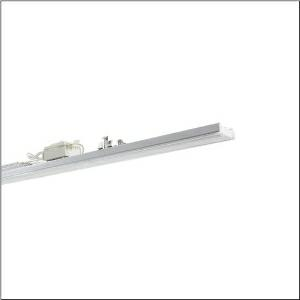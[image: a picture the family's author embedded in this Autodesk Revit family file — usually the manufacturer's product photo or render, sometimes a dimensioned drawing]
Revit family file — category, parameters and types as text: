
# Revit family: licross_r__11_recessed_ho_51tl1emv4g5s_f904
name_source: partatom
category: Lighting Fixtures
units: mm (PartAtom-declared; Revit-internal decimal feet)

## family parameters
Cut with Voids When Loaded = No
Host = Face
Light Source = No
Part Type = Normal
Room Calculation Point = No
Round Connector Dimension = Use Diameter
Shared = No

## types (1)
- --- (1 x LED, 16830 lm, 89.2 W, 4000K)
    Apparent Load = 89 VA
    CIE Flux Codes = 85 95 99 100 100
    Color Rendering = 80
    Color Temperature = 4000K
    Default Elevation = 1800 mm
    Description = Licross® 11 Recessed HO, luminaire insert, of sheet steel, coil coated, white, length: 2.250mm, width: 66mm, height: 67mm, LED rated luminous flux: 16.830lm, light colour: 840, control gear: ON/OFF Multilumen, with plug, 3-pole, with phase selection, mains connection: 220..240V, AC, 50/60Hz, rated input power: 89W, internal wiring halogen-free, primary light control with lens, of plastic, primary optical cover: cover, of PMMA, light emission: direct distribution, primary light characteristic: symmetric, protection rating (complete): IP40, insulation class (complete): insulation class I (protective earthing), certification: CE, ENEC, VDE, UKCA, protection symbol: D if used in an environment without relevant dust loads with corresponding accessories, impact resistance: IK06, permissible ambient temperature for indoor applications: -35..+35°C, corresponds to IFS (International Featured Standards) requirements for safety and quality in the food industry, reducing of maximum allowable ambient temperature of 5°C with ceiling mounting, packaging unit: 1 piece
    Height = 58 mm
    Lamp = 1 x LED
    Lamp Light Flux = 16830 lm
    Lamp Power = 89.2 W
    Lamp count = 1
    Length = 2250 mm
    Luminous efficacy = 189 lm/W
    Manufacturer = Siteco
    ModVariant = No
    Model = 51TL1EMV4G5S
    Mounting Place = Ceiling
    Mounting Type = Pendant
    Number of Poles = 1
    OnlyDefault = Yes
    Power Factor = 1
    Product Name = Licross® 11 Recessed HO
    Product group = luminaire insert | ceiling pendant
    ProductGroupID = 902
    Protection Class = Protection class I
    Protection Degree = IP 40
    RLX_Detail_Level = 1
    RLX_Emergency_Light_Flux = 0 lm
    RLX_Emergency_Type = 0
    RLX_Emergency_Type_DB = No
    RlxData = <blob elided: 27177 chars, md5=9e3826f6>
    Socket = socket
    Standby Power = 0 W
    System Light Flux = 16830 lm
    System Power = 89 W
    Type Comments = factory setting: luminous flux: 100 % | (A | C | E) | 210 mA
    Type Image = l_1296930.jpg
    URL = http://relux.com
    VarID = @adj_105775
    Voltage = 0 V
    Weight = 0.00 kg
    Width = 66 mm

## geometry (parser evidence)
native form markers: Blend x4, Sweep x9
no freeform markers — native parametric forms only
